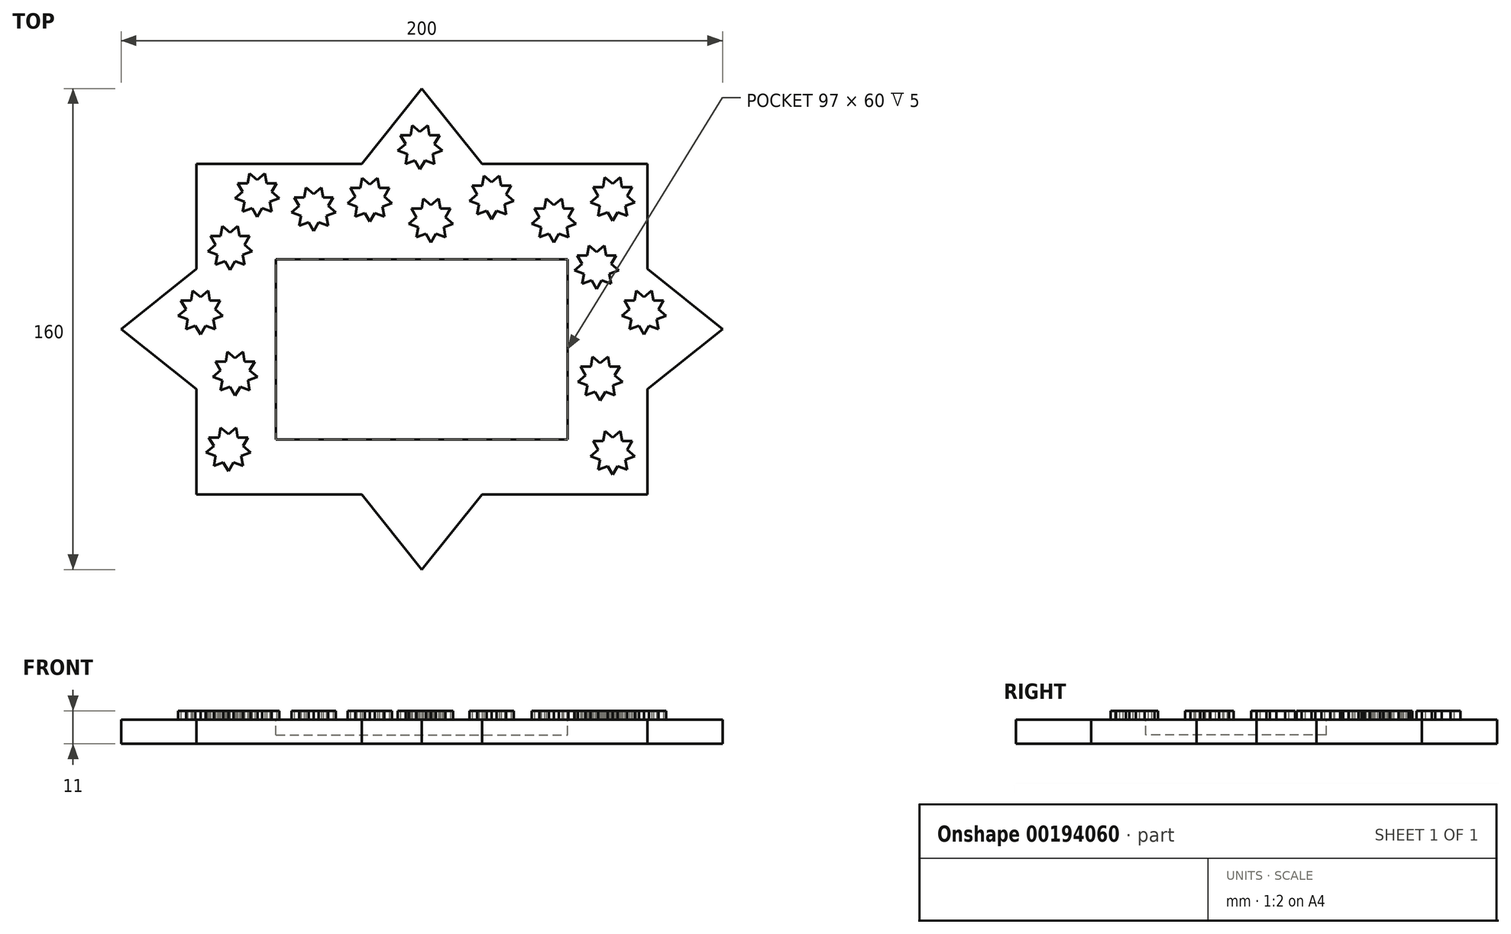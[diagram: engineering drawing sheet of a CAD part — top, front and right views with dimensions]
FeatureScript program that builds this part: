
annotation { "Feature Type Name" : "Feature", "Feature Type Description" : "" }
export const myFeature = defineFeature(function(context is Context, id is Id, definition is map)
    precondition{}
    {
        {
            var Q0;
            Q0=qCreatedBy(makeId("Top.planeOp"),FACE);
            var sketch = newSketch(context, id + "F0", { "sketchPlane" : qUnion([Q0])});
            skLineSegment(sketch, "E0.bottom", {"start": v(75, 55) * mm, "end": v(20, 55) * mm});
            skLineSegment(sketch, "E0.top", {"start": v(75, -55) * mm, "end": v(20, -55) * mm});
            skLineSegment(sketch, "E0.left", {"start": v(75, 55) * mm, "end": v(75, 20) * mm});
            skLineSegment(sketch, "E0.right", {"start": v(-75, 55) * mm, "end": v(-75, 20) * mm});
            skLineSegment(sketch, "E1", {"start": v(75, 20) * mm, "end": v(100, 0) * mm});
            skLineSegment(sketch, "E2", {"start": v(-20, 55) * mm, "end": v(0, 80) * mm});
            skLineSegment(sketch, "E3", {"start": v(0, 80) * mm, "end": v(20, 55) * mm});
            skLineSegment(sketch, "E4.MirrorCS", {"start": v(-20, -55) * mm, "end": v(0, -80) * mm});
            skLineSegment(sketch, "E5.MirrorCS", {"start": v(0, -80) * mm, "end": v(20, -55) * mm});
            skLineSegment(sketch, "E6.MirrorCS", {"start": v(75, -20) * mm, "end": v(100, 0) * mm});
            skLineSegment(sketch, "E7.MirrorCS", {"start": v(-75, 20) * mm, "end": v(-100, 0) * mm});
            skLineSegment(sketch, "E8.MirrorCS", {"start": v(-75, -20) * mm, "end": v(-100, 0) * mm});
            skLineSegment(sketch, "E9.trimOffspring", {"start": v(-75, -20) * mm, "end": v(-75, -55) * mm});
            skLineSegment(sketch, "E10.trimOffspring", {"start": v(75, -20) * mm, "end": v(75, -55) * mm});
            skLineSegment(sketch, "E11.trimOffspring", {"start": v(-20, -55) * mm, "end": v(-75, -55) * mm});
            skLineSegment(sketch, "E12.trimOffspring", {"start": v(-20, 55) * mm, "end": v(-75, 55) * mm});
            skPoint(sketch, "E13.MirrorCS.end.orphan", {"position": v(75, 34.57) * mm});
            skPoint(sketch, "E13.MirrorCS.start.orphan", {"position": v(100, 0) * mm});
            skPoint(sketch, "E14.orphan", {"position": v(75, -34.57) * mm});
            skSolve(sketch);
        }
        {
            var Q0;
            Q0=qSketchRegion(id+"F0",true);
            extrude(context, id + "F1", {"entities" : qUnion([Q0]), "endBound" : BoundingType.SYMMETRIC, "depth" : 8 * mm});
        }
        {
            var Q0;
            Q0=makeQuery(id+"F1.opExtrude","CAP_FACE",FACE,{"disambiguationData":[OSD([sQuery(id+"F0.wireOp",EDGE,"E0.bottom"),sQuery(id+"F0.wireOp",EDGE,"E0.top"),sQuery(id+"F0.wireOp",EDGE,"E0.left"),sQuery(id+"F0.wireOp",EDGE,"E0.right"),sQuery(id+"F0.wireOp",EDGE,"b7ca5f3b-2874-41bd-b902-1c79f96a0a8620.MirrorC"),sQuery(id+"F0.wireOp",EDGE,"b7ca5f3b-2874-41bd-b902-1c79f96a0a8621.MirrorC"),sQuery(id+"F0.wireOp",EDGE,"b7ca5f3b-2874-41bd-b902-1c79f96a0a8622.MirrorCS"),sQuery(id+"F0.wireOp",EDGE,"b7ca5f3b-2874-41bd-b902-1c79f96a0a8623.MirrorCS"),sQuery(id+"F0.wireOp",EDGE,"b7ca5f3b-2874-41bd-b902-1c79f96a0a8624.MirrorCS"),sQuery(id+"F0.wireOp",EDGE,"b7ca5f3b-2874-41bd-b902-1c79f96a0a8625.MirrorCS"),sQuery(id+"F0.wireOp",EDGE,"70034771-ba44-435e-ab74-29499f25fa1546.MirrorC"),sQuery(id+"F0.wireOp",EDGE,"70034771-ba44-435e-ab74-29499f25fa1547.MirrorCS"),sQuery(id+"F0.wireOp",EDGE,"70034771-ba44-435e-ab74-29499f25fa1548.MirrorC"),sQuery(id+"F0.wireOp",EDGE,"70034771-ba44-435e-ab74-29499f25fa1549.MirrorCS"),sQuery(id+"F0.wireOp",EDGE,"70034771-ba44-435e-ab74-29499f25fa1550.MirrorCS"),sQuery(id+"F0.wireOp",EDGE,"70034771-ba44-435e-ab74-29499f25fa1551.MirrorCS"),sQuery(id+"F0.wireOp",EDGE,"E1"),sQuery(id+"F0.wireOp",EDGE,"E2"),sQuery(id+"F0.wireOp",EDGE,"E3"),sQuery(id+"F0.wireOp",EDGE,"E4.MirrorCS"),sQuery(id+"F0.wireOp",EDGE,"E5.MirrorCS"),sQuery(id+"F0.wireOp",EDGE,"E6.MirrorCS"),sQuery(id+"F0.wireOp",EDGE,"E7.MirrorCS"),sQuery(id+"F0.wireOp",EDGE,"E8.MirrorCS"),sQuery(id+"F0.wireOp",EDGE,"E9.trimOffspring"),sQuery(id+"F0.wireOp",EDGE,"E10.trimOffspring"),sQuery(id+"F0.wireOp",EDGE,"E11.trimOffspring"),sQuery(id+"F0.wireOp",EDGE,"E12.trimOffspring")])],"isStart":false});
            var sketch = newSketch(context, id + "F2", { "sketchPlane" : qUnion([Q0])});
            skLineSegment(sketch, "E15.1.17", {"start": v(-32.89, -53.98) * mm, "end": v(-68.5, -53.98) * mm, "construction": true});
            skLineSegment(sketch, "E16.2.0", {"start": v(68.25, 44.34) * mm, "end": v(70.82, 42.19) * mm});
            skLineSegment(sketch, "E16.2.1", {"start": v(61.76, 38.89) * mm, "end": v(58.61, 37.74) * mm});
            skPoint(sketch, "E16.2.2", {"position": v(62.15, 39.96) * mm});
            skCircle(sketch, "E16.2.3", {"center": v(63.43, 43.49) * mm, "radius": 3.75 * mm, "construction": true});
            skLineSegment(sketch, "E16.2.4", {"start": v(56.05, 42.19) * mm, "end": v(58.61, 44.34) * mm});
            skLineSegment(sketch, "E16.2.5", {"start": v(68.25, 37.74) * mm, "end": v(65.1, 38.89) * mm});
            skLineSegment(sketch, "E16.2.6", {"start": v(65.1, 38.89) * mm, "end": v(63.43, 35.99) * mm});
            skLineSegment(sketch, "E16.2.7", {"start": v(69.93, 47.24) * mm, "end": v(68.25, 44.34) * mm});
            skLineSegment(sketch, "E16.2.9", {"start": v(56.94, 47.24) * mm, "end": v(60.29, 47.24) * mm});
            skLineSegment(sketch, "E16.2.10", {"start": v(60.87, 50.54) * mm, "end": v(63.43, 48.38) * mm});
            skLineSegment(sketch, "E16.2.11", {"start": v(60.29, 47.24) * mm, "end": v(60.87, 50.54) * mm});
            skLineSegment(sketch, "E16.2.12", {"start": v(70.82, 42.19) * mm, "end": v(67.67, 41.04) * mm});
            skLineSegment(sketch, "E16.2.13", {"start": v(58.61, 37.74) * mm, "end": v(59.2, 41.04) * mm});
            skLineSegment(sketch, "E16.2.14", {"start": v(58.61, 44.34) * mm, "end": v(56.94, 47.24) * mm});
            skLineSegment(sketch, "E16.2.15", {"start": v(59.2, 41.04) * mm, "end": v(56.05, 42.19) * mm});
            skPoint(sketch, "E16.2.16", {"position": v(66.68, 41.61) * mm});
            skPoint(sketch, "E16.2.18", {"position": v(64.72, 39.96) * mm});
            skLineSegment(sketch, "E16.2.19", {"start": v(63.43, 35.99) * mm, "end": v(61.76, 38.89) * mm});
            skLineSegment(sketch, "E16.2.20", {"start": v(63.43, 48.38) * mm, "end": v(66, 50.54) * mm});
            skLineSegment(sketch, "E16.2.21", {"start": v(67.67, 41.04) * mm, "end": v(68.25, 37.74) * mm});
            skLineSegment(sketch, "E16.2.22", {"start": v(66, 50.54) * mm, "end": v(66.58, 47.24) * mm});
            skLineSegment(sketch, "E16.2.23", {"start": v(66.58, 47.24) * mm, "end": v(69.93, 47.24) * mm});
            skArc(sketch, "E16.2.24", {"start": v(66.68, 41.61) * mm, "mid": v(64.1, 47.18) * mm, "end": v(59.73, 42.88) * mm, "construction": true});
            skArc(sketch, "E16.2.25", {"start": v(62.15, 39.96) * mm, "mid": v(63.43, 39.74) * mm, "end": v(64.72, 39.96) * mm, "construction": true});
            skArc(sketch, "E16.2.26", {"start": v(55.56, 44.8) * mm, "mid": v(71.08, 41.22) * mm, "end": v(56.12, 46.67) * mm, "construction": true});
            skLineSegment(sketch, "E17.2.0", {"start": v(48.77, 37.2) * mm, "end": v(51.34, 35.05) * mm});
            skLineSegment(sketch, "E17.2.1", {"start": v(42.28, 31.75) * mm, "end": v(39.13, 30.6) * mm});
            skPoint(sketch, "E17.2.2", {"position": v(42.67, 32.83) * mm});
            skCircle(sketch, "E17.2.3", {"center": v(43.95, 36.35) * mm, "radius": 3.75 * mm, "construction": true});
            skLineSegment(sketch, "E17.2.4", {"start": v(36.57, 35.05) * mm, "end": v(39.13, 37.2) * mm});
            skLineSegment(sketch, "E17.2.5", {"start": v(48.77, 30.6) * mm, "end": v(45.63, 31.75) * mm});
            skLineSegment(sketch, "E17.2.6", {"start": v(45.63, 31.75) * mm, "end": v(43.95, 28.85) * mm});
            skLineSegment(sketch, "E17.2.7", {"start": v(50.45, 40.1) * mm, "end": v(48.77, 37.2) * mm});
            skLineSegment(sketch, "E17.2.9", {"start": v(37.46, 40.1) * mm, "end": v(40.8, 40.1) * mm});
            skLineSegment(sketch, "E17.2.10", {"start": v(41.39, 43.4) * mm, "end": v(43.95, 41.25) * mm});
            skLineSegment(sketch, "E17.2.11", {"start": v(40.8, 40.1) * mm, "end": v(41.39, 43.4) * mm});
            skLineSegment(sketch, "E17.2.12", {"start": v(51.34, 35.05) * mm, "end": v(48.2, 33.9) * mm});
            skLineSegment(sketch, "E17.2.13", {"start": v(39.13, 30.6) * mm, "end": v(39.71, 33.9) * mm});
            skLineSegment(sketch, "E17.2.14", {"start": v(39.13, 37.2) * mm, "end": v(37.46, 40.1) * mm});
            skLineSegment(sketch, "E17.2.15", {"start": v(39.71, 33.9) * mm, "end": v(36.57, 35.05) * mm});
            skPoint(sketch, "E17.2.16", {"position": v(47.2, 34.47) * mm});
            skPoint(sketch, "E17.2.18", {"position": v(45.23, 32.83) * mm});
            skLineSegment(sketch, "E17.2.19", {"start": v(43.95, 28.85) * mm, "end": v(42.28, 31.75) * mm});
            skLineSegment(sketch, "E17.2.20", {"start": v(43.95, 41.25) * mm, "end": v(46.52, 43.4) * mm});
            skLineSegment(sketch, "E17.2.21", {"start": v(48.2, 33.9) * mm, "end": v(48.77, 30.6) * mm});
            skLineSegment(sketch, "E17.2.22", {"start": v(46.52, 43.4) * mm, "end": v(47.1, 40.1) * mm});
            skLineSegment(sketch, "E17.2.23", {"start": v(47.1, 40.1) * mm, "end": v(50.45, 40.1) * mm});
            skArc(sketch, "E17.2.24", {"start": v(47.2, 34.47) * mm, "mid": v(44.63, 40.04) * mm, "end": v(40.25, 35.74) * mm, "construction": true});
            skArc(sketch, "E17.2.25", {"start": v(42.67, 32.83) * mm, "mid": v(43.95, 32.6) * mm, "end": v(45.23, 32.83) * mm, "construction": true});
            skArc(sketch, "E17.2.26", {"start": v(36.08, 37.66) * mm, "mid": v(51.6, 34.09) * mm, "end": v(36.64, 39.54) * mm, "construction": true});
            skLineSegment(sketch, "E18.2.0", {"start": v(28.05, 44.84) * mm, "end": v(30.62, 42.7) * mm});
            skLineSegment(sketch, "E18.2.1", {"start": v(21.56, 39.4) * mm, "end": v(18.41, 38.25) * mm});
            skPoint(sketch, "E18.2.2", {"position": v(21.95, 40.47) * mm});
            skCircle(sketch, "E18.2.3", {"center": v(23.23, 44) * mm, "radius": 3.75 * mm, "construction": true});
            skLineSegment(sketch, "E18.2.4", {"start": v(15.85, 42.7) * mm, "end": v(18.41, 44.84) * mm});
            skLineSegment(sketch, "E18.2.5", {"start": v(28.05, 38.25) * mm, "end": v(24.9, 39.4) * mm});
            skLineSegment(sketch, "E18.2.6", {"start": v(24.9, 39.4) * mm, "end": v(23.23, 36.5) * mm});
            skLineSegment(sketch, "E18.2.7", {"start": v(29.73, 47.74) * mm, "end": v(28.05, 44.84) * mm});
            skLineSegment(sketch, "E18.2.9", {"start": v(16.74, 47.74) * mm, "end": v(20.09, 47.74) * mm});
            skLineSegment(sketch, "E18.2.10", {"start": v(20.67, 51.04) * mm, "end": v(23.23, 48.89) * mm});
            skLineSegment(sketch, "E18.2.11", {"start": v(20.09, 47.74) * mm, "end": v(20.67, 51.04) * mm});
            skLineSegment(sketch, "E18.2.12", {"start": v(30.62, 42.7) * mm, "end": v(27.47, 41.55) * mm});
            skLineSegment(sketch, "E18.2.13", {"start": v(18.41, 38.25) * mm, "end": v(19, 41.55) * mm});
            skLineSegment(sketch, "E18.2.14", {"start": v(18.41, 44.84) * mm, "end": v(16.74, 47.74) * mm});
            skLineSegment(sketch, "E18.2.15", {"start": v(19, 41.55) * mm, "end": v(15.85, 42.7) * mm});
            skPoint(sketch, "E18.2.16", {"position": v(26.48, 42.12) * mm});
            skPoint(sketch, "E18.2.18", {"position": v(24.52, 40.47) * mm});
            skLineSegment(sketch, "E18.2.19", {"start": v(23.23, 36.5) * mm, "end": v(21.56, 39.4) * mm});
            skLineSegment(sketch, "E18.2.20", {"start": v(23.23, 48.89) * mm, "end": v(25.8, 51.04) * mm});
            skLineSegment(sketch, "E18.2.21", {"start": v(27.47, 41.55) * mm, "end": v(28.05, 38.25) * mm});
            skLineSegment(sketch, "E18.2.22", {"start": v(25.8, 51.04) * mm, "end": v(26.38, 47.74) * mm});
            skLineSegment(sketch, "E18.2.23", {"start": v(26.38, 47.74) * mm, "end": v(29.73, 47.74) * mm});
            skArc(sketch, "E18.2.24", {"start": v(26.48, 42.12) * mm, "mid": v(23.9, 47.68) * mm, "end": v(19.53, 43.39) * mm, "construction": true});
            skArc(sketch, "E18.2.25", {"start": v(21.95, 40.47) * mm, "mid": v(23.23, 40.24) * mm, "end": v(24.52, 40.47) * mm, "construction": true});
            skArc(sketch, "E18.2.26", {"start": v(15.36, 45.3) * mm, "mid": v(30.88, 41.73) * mm, "end": v(15.92, 47.18) * mm, "construction": true});
            skLineSegment(sketch, "E19.2.0", {"start": v(4.22, 61.6) * mm, "end": v(6.78, 59.44) * mm});
            skLineSegment(sketch, "E19.2.1", {"start": v(-2.28, 56.14) * mm, "end": v(-5.42, 55) * mm});
            skPoint(sketch, "E19.2.2", {"position": v(-1.89, 57.22) * mm});
            skCircle(sketch, "E19.2.3", {"center": v(-0.6, 60.74) * mm, "radius": 3.75 * mm, "construction": true});
            skLineSegment(sketch, "E19.2.4", {"start": v(-8, 59.44) * mm, "end": v(-5.42, 61.6) * mm});
            skLineSegment(sketch, "E19.2.5", {"start": v(4.22, 55) * mm, "end": v(1.07, 56.14) * mm});
            skLineSegment(sketch, "E19.2.6", {"start": v(1.07, 56.14) * mm, "end": v(-0.6, 53.24) * mm});
            skLineSegment(sketch, "E19.2.7", {"start": v(5.9, 64.5) * mm, "end": v(4.22, 61.6) * mm});
            skLineSegment(sketch, "E19.2.9", {"start": v(-7.1, 64.5) * mm, "end": v(-3.75, 64.5) * mm});
            skLineSegment(sketch, "E19.2.10", {"start": v(-3.17, 67.79) * mm, "end": v(-0.6, 65.64) * mm});
            skLineSegment(sketch, "E19.2.11", {"start": v(-3.75, 64.5) * mm, "end": v(-3.17, 67.79) * mm});
            skLineSegment(sketch, "E19.2.12", {"start": v(6.78, 59.44) * mm, "end": v(3.64, 58.3) * mm});
            skLineSegment(sketch, "E19.2.13", {"start": v(-5.42, 55) * mm, "end": v(-4.84, 58.3) * mm});
            skLineSegment(sketch, "E19.2.14", {"start": v(-5.42, 61.6) * mm, "end": v(-7.1, 64.5) * mm});
            skLineSegment(sketch, "E19.2.15", {"start": v(-4.84, 58.3) * mm, "end": v(-8, 59.44) * mm});
            skPoint(sketch, "E19.2.16", {"position": v(2.64, 58.87) * mm});
            skPoint(sketch, "E19.2.18", {"position": v(0.68, 57.22) * mm});
            skLineSegment(sketch, "E19.2.19", {"start": v(-0.6, 53.24) * mm, "end": v(-2.28, 56.14) * mm});
            skLineSegment(sketch, "E19.2.20", {"start": v(-0.6, 65.64) * mm, "end": v(1.96, 67.79) * mm});
            skLineSegment(sketch, "E19.2.21", {"start": v(3.64, 58.3) * mm, "end": v(4.22, 55) * mm});
            skLineSegment(sketch, "E19.2.22", {"start": v(1.96, 67.79) * mm, "end": v(2.54, 64.5) * mm});
            skLineSegment(sketch, "E19.2.23", {"start": v(2.54, 64.5) * mm, "end": v(5.9, 64.5) * mm});
            skArc(sketch, "E19.2.24", {"start": v(2.64, 58.87) * mm, "mid": v(-1.95, 64.24) * mm, "end": v(-1.76, 57.17) * mm, "construction": true});
            skArc(sketch, "E19.2.25", {"start": v(-1.89, 57.22) * mm, "mid": v(-0.6, 57) * mm, "end": v(0.68, 57.22) * mm, "construction": true});
            skArc(sketch, "E19.2.26", {"start": v(-6.6, 57.02) * mm, "mid": v(5.77, 63.76) * mm, "end": v(-7.28, 58.47) * mm, "construction": true});
            skLineSegment(sketch, "E20.2.0", {"start": v(7.88, 37.16) * mm, "end": v(10.44, 35.01) * mm});
            skLineSegment(sketch, "E20.2.1", {"start": v(1.38, 31.71) * mm, "end": v(-1.76, 30.57) * mm});
            skPoint(sketch, "E20.2.2", {"position": v(1.77, 32.8) * mm});
            skCircle(sketch, "E20.2.3", {"center": v(3.06, 36.31) * mm, "radius": 3.75 * mm, "construction": true});
            skLineSegment(sketch, "E20.2.4", {"start": v(-4.33, 35.01) * mm, "end": v(-1.76, 37.16) * mm});
            skLineSegment(sketch, "E20.2.5", {"start": v(7.88, 30.57) * mm, "end": v(4.73, 31.71) * mm});
            skLineSegment(sketch, "E20.2.6", {"start": v(4.73, 31.71) * mm, "end": v(3.06, 28.81) * mm});
            skLineSegment(sketch, "E20.2.7", {"start": v(9.55, 40.06) * mm, "end": v(7.88, 37.16) * mm});
            skLineSegment(sketch, "E20.2.9", {"start": v(-3.44, 40.06) * mm, "end": v(-0.1, 40.06) * mm});
            skLineSegment(sketch, "E20.2.10", {"start": v(0.5, 43.36) * mm, "end": v(3.06, 41.21) * mm});
            skLineSegment(sketch, "E20.2.11", {"start": v(-0.1, 40.06) * mm, "end": v(0.5, 43.36) * mm});
            skLineSegment(sketch, "E20.2.12", {"start": v(10.44, 35.01) * mm, "end": v(7.3, 33.87) * mm});
            skLineSegment(sketch, "E20.2.13", {"start": v(-1.76, 30.57) * mm, "end": v(-1.18, 33.87) * mm});
            skLineSegment(sketch, "E20.2.14", {"start": v(-1.76, 37.16) * mm, "end": v(-3.44, 40.06) * mm});
            skLineSegment(sketch, "E20.2.15", {"start": v(-1.18, 33.87) * mm, "end": v(-4.33, 35.01) * mm});
            skPoint(sketch, "E20.2.16", {"position": v(6.3, 34.44) * mm});
            skPoint(sketch, "E20.2.18", {"position": v(4.34, 32.8) * mm});
            skLineSegment(sketch, "E20.2.19", {"start": v(3.06, 28.81) * mm, "end": v(1.38, 31.71) * mm});
            skLineSegment(sketch, "E20.2.20", {"start": v(3.06, 41.21) * mm, "end": v(5.62, 43.36) * mm});
            skLineSegment(sketch, "E20.2.21", {"start": v(7.3, 33.87) * mm, "end": v(7.88, 30.57) * mm});
            skLineSegment(sketch, "E20.2.22", {"start": v(5.62, 43.36) * mm, "end": v(6.2, 40.06) * mm});
            skLineSegment(sketch, "E20.2.23", {"start": v(6.2, 40.06) * mm, "end": v(9.55, 40.06) * mm});
            skArc(sketch, "E20.2.24", {"start": v(6.3, 34.44) * mm, "mid": v(3.73, 40) * mm, "end": v(-0.64, 35.7) * mm, "construction": true});
            skArc(sketch, "E20.2.25", {"start": v(1.77, 32.8) * mm, "mid": v(3.06, 32.56) * mm, "end": v(4.34, 32.8) * mm, "construction": true});
            skArc(sketch, "E20.2.26", {"start": v(-4.81, 37.62) * mm, "mid": v(10.7, 34.05) * mm, "end": v(-4.26, 39.5) * mm, "construction": true});
            skLineSegment(sketch, "E21.2.0", {"start": v(-12.5, 44.08) * mm, "end": v(-9.93, 41.93) * mm});
            skLineSegment(sketch, "E21.2.1", {"start": v(-19, 38.63) * mm, "end": v(-22.14, 37.49) * mm});
            skPoint(sketch, "E21.2.2", {"position": v(-18.6, 39.7) * mm});
            skCircle(sketch, "E21.2.3", {"center": v(-17.32, 43.23) * mm, "radius": 3.75 * mm, "construction": true});
            skLineSegment(sketch, "E21.2.4", {"start": v(-24.7, 41.93) * mm, "end": v(-22.14, 44.08) * mm});
            skLineSegment(sketch, "E21.2.5", {"start": v(-12.5, 37.49) * mm, "end": v(-15.64, 38.63) * mm});
            skLineSegment(sketch, "E21.2.6", {"start": v(-15.64, 38.63) * mm, "end": v(-17.32, 35.73) * mm});
            skLineSegment(sketch, "E21.2.7", {"start": v(-10.82, 46.98) * mm, "end": v(-12.5, 44.08) * mm});
            skLineSegment(sketch, "E21.2.9", {"start": v(-23.81, 46.98) * mm, "end": v(-20.47, 46.98) * mm});
            skLineSegment(sketch, "E21.2.10", {"start": v(-19.88, 50.28) * mm, "end": v(-17.32, 48.13) * mm});
            skLineSegment(sketch, "E21.2.11", {"start": v(-20.47, 46.98) * mm, "end": v(-19.88, 50.28) * mm});
            skLineSegment(sketch, "E21.2.12", {"start": v(-9.93, 41.93) * mm, "end": v(-13.08, 40.78) * mm});
            skLineSegment(sketch, "E21.2.13", {"start": v(-22.14, 37.49) * mm, "end": v(-21.56, 40.78) * mm});
            skLineSegment(sketch, "E21.2.14", {"start": v(-22.14, 44.08) * mm, "end": v(-23.81, 46.98) * mm});
            skLineSegment(sketch, "E21.2.15", {"start": v(-21.56, 40.78) * mm, "end": v(-24.7, 41.93) * mm});
            skPoint(sketch, "E21.2.16", {"position": v(-14.07, 41.36) * mm});
            skPoint(sketch, "E21.2.18", {"position": v(-16.04, 39.7) * mm});
            skLineSegment(sketch, "E21.2.19", {"start": v(-17.32, 35.73) * mm, "end": v(-19, 38.63) * mm});
            skLineSegment(sketch, "E21.2.20", {"start": v(-17.32, 48.13) * mm, "end": v(-14.75, 50.28) * mm});
            skLineSegment(sketch, "E21.2.21", {"start": v(-13.08, 40.78) * mm, "end": v(-12.5, 37.49) * mm});
            skLineSegment(sketch, "E21.2.22", {"start": v(-14.75, 50.28) * mm, "end": v(-14.17, 46.98) * mm});
            skLineSegment(sketch, "E21.2.23", {"start": v(-14.17, 46.98) * mm, "end": v(-10.82, 46.98) * mm});
            skArc(sketch, "E21.2.24", {"start": v(-14.07, 41.36) * mm, "mid": v(-16.65, 46.92) * mm, "end": v(-21.02, 42.62) * mm, "construction": true});
            skArc(sketch, "E21.2.25", {"start": v(-18.6, 39.7) * mm, "mid": v(-17.32, 39.48) * mm, "end": v(-16.04, 39.7) * mm, "construction": true});
            skArc(sketch, "E21.2.26", {"start": v(-25.19, 44.54) * mm, "mid": v(-9.67, 40.97) * mm, "end": v(-24.63, 46.42) * mm, "construction": true});
            skLineSegment(sketch, "E22.2.0", {"start": v(-31.15, 40.93) * mm, "end": v(-28.58, 38.78) * mm});
            skLineSegment(sketch, "E22.2.1", {"start": v(-37.64, 35.48) * mm, "end": v(-40.8, 34.34) * mm});
            skPoint(sketch, "E22.2.2", {"position": v(-37.25, 36.56) * mm});
            skCircle(sketch, "E22.2.3", {"center": v(-35.97, 40.08) * mm, "radius": 3.75 * mm, "construction": true});
            skLineSegment(sketch, "E22.2.4", {"start": v(-43.36, 38.78) * mm, "end": v(-40.8, 40.93) * mm});
            skLineSegment(sketch, "E22.2.5", {"start": v(-31.15, 34.34) * mm, "end": v(-34.3, 35.48) * mm});
            skLineSegment(sketch, "E22.2.6", {"start": v(-34.3, 35.48) * mm, "end": v(-35.97, 32.58) * mm});
            skLineSegment(sketch, "E22.2.7", {"start": v(-29.47, 43.83) * mm, "end": v(-31.15, 40.93) * mm});
            skLineSegment(sketch, "E22.2.9", {"start": v(-42.46, 43.83) * mm, "end": v(-39.12, 43.83) * mm});
            skLineSegment(sketch, "E22.2.10", {"start": v(-38.53, 47.13) * mm, "end": v(-35.97, 44.98) * mm});
            skLineSegment(sketch, "E22.2.11", {"start": v(-39.12, 43.83) * mm, "end": v(-38.53, 47.13) * mm});
            skLineSegment(sketch, "E22.2.12", {"start": v(-28.58, 38.78) * mm, "end": v(-31.73, 37.64) * mm});
            skLineSegment(sketch, "E22.2.13", {"start": v(-40.8, 34.34) * mm, "end": v(-40.2, 37.64) * mm});
            skLineSegment(sketch, "E22.2.14", {"start": v(-40.8, 40.93) * mm, "end": v(-42.46, 43.83) * mm});
            skLineSegment(sketch, "E22.2.15", {"start": v(-40.2, 37.64) * mm, "end": v(-43.36, 38.78) * mm});
            skPoint(sketch, "E22.2.16", {"position": v(-32.72, 38.2) * mm});
            skPoint(sketch, "E22.2.18", {"position": v(-34.69, 36.56) * mm});
            skLineSegment(sketch, "E22.2.19", {"start": v(-35.97, 32.58) * mm, "end": v(-37.64, 35.48) * mm});
            skLineSegment(sketch, "E22.2.20", {"start": v(-35.97, 44.98) * mm, "end": v(-33.4, 47.13) * mm});
            skLineSegment(sketch, "E22.2.21", {"start": v(-31.73, 37.64) * mm, "end": v(-31.15, 34.34) * mm});
            skLineSegment(sketch, "E22.2.22", {"start": v(-33.4, 47.13) * mm, "end": v(-32.82, 43.83) * mm});
            skLineSegment(sketch, "E22.2.23", {"start": v(-32.82, 43.83) * mm, "end": v(-29.47, 43.83) * mm});
            skArc(sketch, "E22.2.24", {"start": v(-32.72, 38.2) * mm, "mid": v(-35.3, 43.77) * mm, "end": v(-39.67, 39.48) * mm, "construction": true});
            skArc(sketch, "E22.2.25", {"start": v(-37.25, 36.56) * mm, "mid": v(-35.97, 36.33) * mm, "end": v(-34.69, 36.56) * mm, "construction": true});
            skArc(sketch, "E22.2.26", {"start": v(-43.84, 41.4) * mm, "mid": v(-28.32, 37.82) * mm, "end": v(-43.28, 43.27) * mm, "construction": true});
            skLineSegment(sketch, "E23.2.0", {"start": v(-49.95, 45.64) * mm, "end": v(-47.38, 43.48) * mm});
            skLineSegment(sketch, "E23.2.1", {"start": v(-56.44, 40.19) * mm, "end": v(-59.59, 39.04) * mm});
            skPoint(sketch, "E23.2.2", {"position": v(-56.05, 41.26) * mm});
            skCircle(sketch, "E23.2.3", {"center": v(-54.77, 44.79) * mm, "radius": 3.75 * mm, "construction": true});
            skLineSegment(sketch, "E23.2.4", {"start": v(-62.15, 43.48) * mm, "end": v(-59.59, 45.64) * mm});
            skLineSegment(sketch, "E23.2.5", {"start": v(-49.95, 39.04) * mm, "end": v(-53.1, 40.19) * mm});
            skLineSegment(sketch, "E23.2.6", {"start": v(-53.1, 40.19) * mm, "end": v(-54.77, 37.29) * mm});
            skLineSegment(sketch, "E23.2.7", {"start": v(-48.27, 48.54) * mm, "end": v(-49.95, 45.64) * mm});
            skLineSegment(sketch, "E23.2.9", {"start": v(-61.26, 48.54) * mm, "end": v(-57.91, 48.54) * mm});
            skLineSegment(sketch, "E23.2.10", {"start": v(-57.33, 51.83) * mm, "end": v(-54.77, 49.68) * mm});
            skLineSegment(sketch, "E23.2.11", {"start": v(-57.91, 48.54) * mm, "end": v(-57.33, 51.83) * mm});
            skLineSegment(sketch, "E23.2.12", {"start": v(-47.38, 43.48) * mm, "end": v(-50.53, 42.34) * mm});
            skLineSegment(sketch, "E23.2.13", {"start": v(-59.59, 39.04) * mm, "end": v(-59, 42.34) * mm});
            skLineSegment(sketch, "E23.2.14", {"start": v(-59.59, 45.64) * mm, "end": v(-61.26, 48.54) * mm});
            skLineSegment(sketch, "E23.2.15", {"start": v(-59, 42.34) * mm, "end": v(-62.15, 43.48) * mm});
            skPoint(sketch, "E23.2.16", {"position": v(-51.52, 42.91) * mm});
            skPoint(sketch, "E23.2.18", {"position": v(-53.48, 41.26) * mm});
            skLineSegment(sketch, "E23.2.19", {"start": v(-54.77, 37.29) * mm, "end": v(-56.44, 40.19) * mm});
            skLineSegment(sketch, "E23.2.20", {"start": v(-54.77, 49.68) * mm, "end": v(-52.2, 51.83) * mm});
            skLineSegment(sketch, "E23.2.21", {"start": v(-50.53, 42.34) * mm, "end": v(-49.95, 39.04) * mm});
            skLineSegment(sketch, "E23.2.22", {"start": v(-52.2, 51.83) * mm, "end": v(-51.62, 48.54) * mm});
            skLineSegment(sketch, "E23.2.23", {"start": v(-51.62, 48.54) * mm, "end": v(-48.27, 48.54) * mm});
            skArc(sketch, "E23.2.24", {"start": v(-51.52, 42.91) * mm, "mid": v(-54.1, 48.48) * mm, "end": v(-58.47, 44.18) * mm, "construction": true});
            skArc(sketch, "E23.2.25", {"start": v(-56.05, 41.26) * mm, "mid": v(-54.77, 41.04) * mm, "end": v(-53.48, 41.26) * mm, "construction": true});
            skArc(sketch, "E23.2.26", {"start": v(-62.64, 46.1) * mm, "mid": v(-47.12, 42.52) * mm, "end": v(-62.08, 47.97) * mm, "construction": true});
            skLineSegment(sketch, "E24.2.0", {"start": v(-58.97, 28) * mm, "end": v(-56.4, 25.85) * mm});
            skLineSegment(sketch, "E24.2.1", {"start": v(-65.46, 22.55) * mm, "end": v(-68.6, 21.4) * mm});
            skPoint(sketch, "E24.2.2", {"position": v(-65.07, 23.63) * mm});
            skCircle(sketch, "E24.2.3", {"center": v(-63.79, 27.15) * mm, "radius": 3.75 * mm, "construction": true});
            skLineSegment(sketch, "E24.2.4", {"start": v(-71.17, 25.85) * mm, "end": v(-68.6, 28) * mm});
            skLineSegment(sketch, "E24.2.5", {"start": v(-58.97, 21.4) * mm, "end": v(-62.11, 22.55) * mm});
            skLineSegment(sketch, "E24.2.6", {"start": v(-62.11, 22.55) * mm, "end": v(-63.79, 19.65) * mm});
            skLineSegment(sketch, "E24.2.7", {"start": v(-57.3, 30.9) * mm, "end": v(-58.97, 28) * mm});
            skLineSegment(sketch, "E24.2.9", {"start": v(-70.28, 30.9) * mm, "end": v(-66.93, 30.9) * mm});
            skLineSegment(sketch, "E24.2.10", {"start": v(-66.35, 34.2) * mm, "end": v(-63.79, 32.05) * mm});
            skLineSegment(sketch, "E24.2.11", {"start": v(-66.93, 30.9) * mm, "end": v(-66.35, 34.2) * mm});
            skLineSegment(sketch, "E24.2.12", {"start": v(-56.4, 25.85) * mm, "end": v(-59.55, 24.7) * mm});
            skLineSegment(sketch, "E24.2.13", {"start": v(-68.6, 21.4) * mm, "end": v(-68.03, 24.7) * mm});
            skLineSegment(sketch, "E24.2.14", {"start": v(-68.6, 28) * mm, "end": v(-70.28, 30.9) * mm});
            skLineSegment(sketch, "E24.2.15", {"start": v(-68.03, 24.7) * mm, "end": v(-71.17, 25.85) * mm});
            skPoint(sketch, "E24.2.16", {"position": v(-60.54, 25.28) * mm});
            skPoint(sketch, "E24.2.18", {"position": v(-62.5, 23.63) * mm});
            skLineSegment(sketch, "E24.2.19", {"start": v(-63.79, 19.65) * mm, "end": v(-65.46, 22.55) * mm});
            skLineSegment(sketch, "E24.2.20", {"start": v(-63.79, 32.05) * mm, "end": v(-61.22, 34.2) * mm});
            skLineSegment(sketch, "E24.2.21", {"start": v(-59.55, 24.7) * mm, "end": v(-58.97, 21.4) * mm});
            skLineSegment(sketch, "E24.2.22", {"start": v(-61.22, 34.2) * mm, "end": v(-60.64, 30.9) * mm});
            skLineSegment(sketch, "E24.2.23", {"start": v(-60.64, 30.9) * mm, "end": v(-57.3, 30.9) * mm});
            skArc(sketch, "E24.2.24", {"start": v(-60.54, 25.28) * mm, "mid": v(-63.11, 30.84) * mm, "end": v(-67.49, 26.54) * mm, "construction": true});
            skArc(sketch, "E24.2.25", {"start": v(-65.07, 23.63) * mm, "mid": v(-63.79, 23.4) * mm, "end": v(-62.5, 23.63) * mm, "construction": true});
            skArc(sketch, "E24.2.26", {"start": v(-71.66, 28.46) * mm, "mid": v(-56.14, 24.89) * mm, "end": v(-71.1, 30.34) * mm, "construction": true});
            skLineSegment(sketch, "E25.2.0", {"start": v(-68.8, 6.6) * mm, "end": v(-66.24, 4.44) * mm});
            skLineSegment(sketch, "E25.2.1", {"start": v(-75.3, 1.15) * mm, "end": v(-78.44, 0) * mm});
            skPoint(sketch, "E25.2.2", {"position": v(-74.9, 2.22) * mm});
            skCircle(sketch, "E25.2.3", {"center": v(-73.62, 5.75) * mm, "radius": 3.75 * mm, "construction": true});
            skLineSegment(sketch, "E25.2.4", {"start": v(-81, 4.44) * mm, "end": v(-78.44, 6.6) * mm});
            skLineSegment(sketch, "E25.2.5", {"start": v(-68.8, 0) * mm, "end": v(-71.95, 1.15) * mm});
            skLineSegment(sketch, "E25.2.6", {"start": v(-71.95, 1.15) * mm, "end": v(-73.62, -1.75) * mm});
            skLineSegment(sketch, "E25.2.7", {"start": v(-67.13, 9.5) * mm, "end": v(-68.8, 6.6) * mm});
            skLineSegment(sketch, "E25.2.9", {"start": v(-80.12, 9.5) * mm, "end": v(-76.77, 9.5) * mm});
            skLineSegment(sketch, "E25.2.10", {"start": v(-76.19, 12.8) * mm, "end": v(-73.62, 10.64) * mm});
            skLineSegment(sketch, "E25.2.11", {"start": v(-76.77, 9.5) * mm, "end": v(-76.19, 12.8) * mm});
            skLineSegment(sketch, "E25.2.12", {"start": v(-66.24, 4.44) * mm, "end": v(-69.38, 3.3) * mm});
            skLineSegment(sketch, "E25.2.13", {"start": v(-78.44, 0) * mm, "end": v(-77.86, 3.3) * mm});
            skLineSegment(sketch, "E25.2.14", {"start": v(-78.44, 6.6) * mm, "end": v(-80.12, 9.5) * mm});
            skLineSegment(sketch, "E25.2.15", {"start": v(-77.86, 3.3) * mm, "end": v(-81, 4.44) * mm});
            skPoint(sketch, "E25.2.16", {"position": v(-70.37, 3.87) * mm});
            skPoint(sketch, "E25.2.18", {"position": v(-72.34, 2.22) * mm});
            skLineSegment(sketch, "E25.2.19", {"start": v(-73.62, -1.75) * mm, "end": v(-75.3, 1.15) * mm});
            skLineSegment(sketch, "E25.2.20", {"start": v(-73.62, 10.64) * mm, "end": v(-71.06, 12.8) * mm});
            skLineSegment(sketch, "E25.2.21", {"start": v(-69.38, 3.3) * mm, "end": v(-68.8, 0) * mm});
            skLineSegment(sketch, "E25.2.22", {"start": v(-71.06, 12.8) * mm, "end": v(-70.47, 9.5) * mm});
            skLineSegment(sketch, "E25.2.23", {"start": v(-70.47, 9.5) * mm, "end": v(-67.13, 9.5) * mm});
            skArc(sketch, "E25.2.24", {"start": v(-70.37, 3.87) * mm, "mid": v(-72.95, 9.43) * mm, "end": v(-77.32, 5.14) * mm, "construction": true});
            skArc(sketch, "E25.2.25", {"start": v(-74.9, 2.22) * mm, "mid": v(-73.62, 2) * mm, "end": v(-72.34, 2.22) * mm, "construction": true});
            skArc(sketch, "E25.2.26", {"start": v(-81.5, 7.05) * mm, "mid": v(-65.97, 3.48) * mm, "end": v(-80.94, 8.93) * mm, "construction": true});
            skLineSegment(sketch, "E26.2.0", {"start": v(-57.25, -13.77) * mm, "end": v(-54.69, -15.92) * mm});
            skLineSegment(sketch, "E26.2.1", {"start": v(-63.75, -19.22) * mm, "end": v(-66.9, -20.36) * mm});
            skPoint(sketch, "E26.2.2", {"position": v(-63.35, -18.14) * mm});
            skCircle(sketch, "E26.2.3", {"center": v(-62.07, -14.62) * mm, "radius": 3.75 * mm, "construction": true});
            skLineSegment(sketch, "E26.2.4", {"start": v(-69.46, -15.92) * mm, "end": v(-66.9, -13.77) * mm});
            skLineSegment(sketch, "E26.2.5", {"start": v(-57.25, -20.36) * mm, "end": v(-60.4, -19.22) * mm});
            skLineSegment(sketch, "E26.2.6", {"start": v(-60.4, -19.22) * mm, "end": v(-62.07, -22.12) * mm});
            skLineSegment(sketch, "E26.2.7", {"start": v(-55.58, -10.87) * mm, "end": v(-57.25, -13.77) * mm});
            skLineSegment(sketch, "E26.2.9", {"start": v(-68.57, -10.87) * mm, "end": v(-65.22, -10.87) * mm});
            skLineSegment(sketch, "E26.2.10", {"start": v(-64.64, -7.57) * mm, "end": v(-62.07, -9.72) * mm});
            skLineSegment(sketch, "E26.2.11", {"start": v(-65.22, -10.87) * mm, "end": v(-64.64, -7.57) * mm});
            skLineSegment(sketch, "E26.2.12", {"start": v(-54.69, -15.92) * mm, "end": v(-57.83, -17.07) * mm});
            skLineSegment(sketch, "E26.2.13", {"start": v(-66.9, -20.36) * mm, "end": v(-66.31, -17.07) * mm});
            skLineSegment(sketch, "E26.2.14", {"start": v(-66.9, -13.77) * mm, "end": v(-68.57, -10.87) * mm});
            skLineSegment(sketch, "E26.2.15", {"start": v(-66.31, -17.07) * mm, "end": v(-69.46, -15.92) * mm});
            skPoint(sketch, "E26.2.16", {"position": v(-58.82, -16.5) * mm});
            skPoint(sketch, "E26.2.18", {"position": v(-60.79, -18.14) * mm});
            skLineSegment(sketch, "E26.2.19", {"start": v(-62.07, -22.12) * mm, "end": v(-63.75, -19.22) * mm});
            skLineSegment(sketch, "E26.2.20", {"start": v(-62.07, -9.72) * mm, "end": v(-59.5, -7.57) * mm});
            skLineSegment(sketch, "E26.2.21", {"start": v(-57.83, -17.07) * mm, "end": v(-57.25, -20.36) * mm});
            skLineSegment(sketch, "E26.2.22", {"start": v(-59.5, -7.57) * mm, "end": v(-58.93, -10.87) * mm});
            skLineSegment(sketch, "E26.2.23", {"start": v(-58.93, -10.87) * mm, "end": v(-55.58, -10.87) * mm});
            skArc(sketch, "E26.2.24", {"start": v(-58.82, -16.5) * mm, "mid": v(-61.4, -10.93) * mm, "end": v(-65.77, -15.23) * mm, "construction": true});
            skArc(sketch, "E26.2.25", {"start": v(-63.35, -18.14) * mm, "mid": v(-62.07, -18.37) * mm, "end": v(-60.79, -18.14) * mm, "construction": true});
            skArc(sketch, "E26.2.26", {"start": v(-69.94, -13.31) * mm, "mid": v(-54.42, -16.88) * mm, "end": v(-69.39, -11.43) * mm, "construction": true});
            skLineSegment(sketch, "E27.2.0", {"start": v(62.94, 21.64) * mm, "end": v(65.5, 19.49) * mm});
            skLineSegment(sketch, "E27.2.1", {"start": v(56.45, 16.19) * mm, "end": v(53.3, 15.04) * mm});
            skPoint(sketch, "E27.2.2", {"position": v(56.84, 17.27) * mm});
            skCircle(sketch, "E27.2.3", {"center": v(58.12, 20.79) * mm, "radius": 3.75 * mm, "construction": true});
            skLineSegment(sketch, "E27.2.4", {"start": v(50.74, 19.49) * mm, "end": v(53.3, 21.64) * mm});
            skLineSegment(sketch, "E27.2.5", {"start": v(62.94, 15.04) * mm, "end": v(59.8, 16.19) * mm});
            skLineSegment(sketch, "E27.2.6", {"start": v(59.8, 16.19) * mm, "end": v(58.12, 13.29) * mm});
            skLineSegment(sketch, "E27.2.7", {"start": v(64.62, 24.54) * mm, "end": v(62.94, 21.64) * mm});
            skLineSegment(sketch, "E27.2.9", {"start": v(51.63, 24.54) * mm, "end": v(54.98, 24.54) * mm});
            skLineSegment(sketch, "E27.2.10", {"start": v(55.56, 27.84) * mm, "end": v(58.12, 25.68) * mm});
            skLineSegment(sketch, "E27.2.11", {"start": v(54.98, 24.54) * mm, "end": v(55.56, 27.84) * mm});
            skLineSegment(sketch, "E27.2.12", {"start": v(65.5, 19.49) * mm, "end": v(62.36, 18.34) * mm});
            skLineSegment(sketch, "E27.2.13", {"start": v(53.3, 15.04) * mm, "end": v(53.88, 18.34) * mm});
            skLineSegment(sketch, "E27.2.14", {"start": v(53.3, 21.64) * mm, "end": v(51.63, 24.54) * mm});
            skLineSegment(sketch, "E27.2.15", {"start": v(53.88, 18.34) * mm, "end": v(50.74, 19.49) * mm});
            skPoint(sketch, "E27.2.16", {"position": v(61.37, 18.91) * mm});
            skPoint(sketch, "E27.2.18", {"position": v(59.4, 17.27) * mm});
            skLineSegment(sketch, "E27.2.19", {"start": v(58.12, 13.29) * mm, "end": v(56.45, 16.19) * mm});
            skLineSegment(sketch, "E27.2.20", {"start": v(58.12, 25.68) * mm, "end": v(60.69, 27.84) * mm});
            skLineSegment(sketch, "E27.2.21", {"start": v(62.36, 18.34) * mm, "end": v(62.94, 15.04) * mm});
            skLineSegment(sketch, "E27.2.22", {"start": v(60.69, 27.84) * mm, "end": v(61.27, 24.54) * mm});
            skLineSegment(sketch, "E27.2.23", {"start": v(61.27, 24.54) * mm, "end": v(64.62, 24.54) * mm});
            skArc(sketch, "E27.2.24", {"start": v(61.37, 18.91) * mm, "mid": v(58.8, 24.48) * mm, "end": v(54.42, 20.18) * mm, "construction": true});
            skArc(sketch, "E27.2.25", {"start": v(56.84, 17.27) * mm, "mid": v(58.12, 17.04) * mm, "end": v(59.4, 17.27) * mm, "construction": true});
            skArc(sketch, "E27.2.26", {"start": v(50.25, 22.1) * mm, "mid": v(65.77, 18.53) * mm, "end": v(50.8, 23.98) * mm, "construction": true});
            skLineSegment(sketch, "E28.2.0", {"start": v(78.7, 6.6) * mm, "end": v(81.27, 4.44) * mm});
            skLineSegment(sketch, "E28.2.1", {"start": v(72.21, 1.15) * mm, "end": v(69.06, 0) * mm});
            skPoint(sketch, "E28.2.2", {"position": v(72.6, 2.22) * mm});
            skCircle(sketch, "E28.2.3", {"center": v(73.89, 5.75) * mm, "radius": 3.75 * mm, "construction": true});
            skLineSegment(sketch, "E28.2.4", {"start": v(66.5, 4.44) * mm, "end": v(69.06, 6.6) * mm});
            skLineSegment(sketch, "E28.2.5", {"start": v(78.7, 0) * mm, "end": v(75.56, 1.15) * mm});
            skLineSegment(sketch, "E28.2.6", {"start": v(75.56, 1.15) * mm, "end": v(73.89, -1.75) * mm});
            skLineSegment(sketch, "E28.2.7", {"start": v(80.38, 9.5) * mm, "end": v(78.7, 6.6) * mm});
            skLineSegment(sketch, "E28.2.9", {"start": v(67.4, 9.5) * mm, "end": v(70.74, 9.5) * mm});
            skLineSegment(sketch, "E28.2.10", {"start": v(71.32, 12.8) * mm, "end": v(73.89, 10.64) * mm});
            skLineSegment(sketch, "E28.2.11", {"start": v(70.74, 9.5) * mm, "end": v(71.32, 12.8) * mm});
            skLineSegment(sketch, "E28.2.12", {"start": v(81.27, 4.44) * mm, "end": v(78.12, 3.3) * mm});
            skLineSegment(sketch, "E28.2.13", {"start": v(69.06, 0) * mm, "end": v(69.65, 3.3) * mm});
            skLineSegment(sketch, "E28.2.14", {"start": v(69.06, 6.6) * mm, "end": v(67.4, 9.5) * mm});
            skLineSegment(sketch, "E28.2.15", {"start": v(69.65, 3.3) * mm, "end": v(66.5, 4.44) * mm});
            skPoint(sketch, "E28.2.16", {"position": v(77.13, 3.87) * mm});
            skPoint(sketch, "E28.2.18", {"position": v(75.17, 2.22) * mm});
            skLineSegment(sketch, "E28.2.19", {"start": v(73.89, -1.75) * mm, "end": v(72.21, 1.15) * mm});
            skLineSegment(sketch, "E28.2.20", {"start": v(73.89, 10.64) * mm, "end": v(76.45, 12.8) * mm});
            skLineSegment(sketch, "E28.2.21", {"start": v(78.12, 3.3) * mm, "end": v(78.7, 0) * mm});
            skLineSegment(sketch, "E28.2.22", {"start": v(76.45, 12.8) * mm, "end": v(77.03, 9.5) * mm});
            skLineSegment(sketch, "E28.2.23", {"start": v(77.03, 9.5) * mm, "end": v(80.38, 9.5) * mm});
            skArc(sketch, "E28.2.24", {"start": v(77.13, 3.87) * mm, "mid": v(74.56, 9.43) * mm, "end": v(70.18, 5.14) * mm, "construction": true});
            skArc(sketch, "E28.2.25", {"start": v(72.6, 2.22) * mm, "mid": v(73.89, 2) * mm, "end": v(75.17, 2.22) * mm, "construction": true});
            skArc(sketch, "E28.2.26", {"start": v(66.01, 7.05) * mm, "mid": v(81.54, 3.48) * mm, "end": v(66.57, 8.93) * mm, "construction": true});
            skLineSegment(sketch, "E29.2.0", {"start": v(64.15, -15.39) * mm, "end": v(66.72, -17.54) * mm});
            skLineSegment(sketch, "E29.2.1", {"start": v(57.66, -20.84) * mm, "end": v(54.51, -21.98) * mm});
            skPoint(sketch, "E29.2.2", {"position": v(58.05, -19.76) * mm});
            skCircle(sketch, "E29.2.3", {"center": v(59.33, -16.24) * mm, "radius": 3.75 * mm, "construction": true});
            skLineSegment(sketch, "E29.2.4", {"start": v(51.95, -17.54) * mm, "end": v(54.51, -15.39) * mm});
            skLineSegment(sketch, "E29.2.5", {"start": v(64.15, -21.98) * mm, "end": v(61, -20.84) * mm});
            skLineSegment(sketch, "E29.2.6", {"start": v(61, -20.84) * mm, "end": v(59.33, -23.74) * mm});
            skLineSegment(sketch, "E29.2.7", {"start": v(65.83, -12.49) * mm, "end": v(64.15, -15.39) * mm});
            skLineSegment(sketch, "E29.2.9", {"start": v(52.84, -12.49) * mm, "end": v(56.18, -12.49) * mm});
            skLineSegment(sketch, "E29.2.10", {"start": v(56.77, -9.2) * mm, "end": v(59.33, -11.34) * mm});
            skLineSegment(sketch, "E29.2.11", {"start": v(56.18, -12.49) * mm, "end": v(56.77, -9.2) * mm});
            skLineSegment(sketch, "E29.2.12", {"start": v(66.72, -17.54) * mm, "end": v(63.57, -18.69) * mm});
            skLineSegment(sketch, "E29.2.13", {"start": v(54.51, -21.98) * mm, "end": v(55.1, -18.69) * mm});
            skLineSegment(sketch, "E29.2.14", {"start": v(54.51, -15.39) * mm, "end": v(52.84, -12.49) * mm});
            skLineSegment(sketch, "E29.2.15", {"start": v(55.1, -18.69) * mm, "end": v(51.95, -17.54) * mm});
            skPoint(sketch, "E29.2.16", {"position": v(62.58, -18.11) * mm});
            skPoint(sketch, "E29.2.18", {"position": v(60.61, -19.76) * mm});
            skLineSegment(sketch, "E29.2.19", {"start": v(59.33, -23.74) * mm, "end": v(57.66, -20.84) * mm});
            skLineSegment(sketch, "E29.2.20", {"start": v(59.33, -11.34) * mm, "end": v(61.9, -9.2) * mm});
            skLineSegment(sketch, "E29.2.21", {"start": v(63.57, -18.69) * mm, "end": v(64.15, -21.98) * mm});
            skLineSegment(sketch, "E29.2.22", {"start": v(61.9, -9.2) * mm, "end": v(62.48, -12.49) * mm});
            skLineSegment(sketch, "E29.2.23", {"start": v(62.48, -12.49) * mm, "end": v(65.83, -12.49) * mm});
            skArc(sketch, "E29.2.24", {"start": v(62.58, -18.11) * mm, "mid": v(60, -12.55) * mm, "end": v(55.63, -16.85) * mm, "construction": true});
            skArc(sketch, "E29.2.25", {"start": v(58.05, -19.76) * mm, "mid": v(59.33, -19.99) * mm, "end": v(60.61, -19.76) * mm, "construction": true});
            skArc(sketch, "E29.2.26", {"start": v(51.46, -14.93) * mm, "mid": v(66.98, -18.5) * mm, "end": v(52.02, -13.05) * mm, "construction": true});
            skLineSegment(sketch, "E30.2.0", {"start": v(-59.52, -38.94) * mm, "end": v(-56.95, -41.1) * mm});
            skLineSegment(sketch, "E30.2.1", {"start": v(-66.01, -44.4) * mm, "end": v(-69.16, -45.54) * mm});
            skPoint(sketch, "E30.2.2", {"position": v(-65.62, -43.32) * mm});
            skCircle(sketch, "E30.2.3", {"center": v(-64.34, -39.8) * mm, "radius": 3.75 * mm, "construction": true});
            skLineSegment(sketch, "E30.2.4", {"start": v(-71.73, -41.1) * mm, "end": v(-69.16, -38.94) * mm});
            skLineSegment(sketch, "E30.2.5", {"start": v(-59.52, -45.54) * mm, "end": v(-62.67, -44.4) * mm});
            skLineSegment(sketch, "E30.2.6", {"start": v(-62.67, -44.4) * mm, "end": v(-64.34, -47.3) * mm});
            skLineSegment(sketch, "E30.2.7", {"start": v(-57.85, -36.04) * mm, "end": v(-59.52, -38.94) * mm});
            skLineSegment(sketch, "E30.2.9", {"start": v(-70.84, -36.04) * mm, "end": v(-67.49, -36.04) * mm});
            skLineSegment(sketch, "E30.2.10", {"start": v(-66.9, -32.75) * mm, "end": v(-64.34, -34.9) * mm});
            skLineSegment(sketch, "E30.2.11", {"start": v(-67.49, -36.04) * mm, "end": v(-66.9, -32.75) * mm});
            skLineSegment(sketch, "E30.2.12", {"start": v(-56.95, -41.1) * mm, "end": v(-60.1, -42.24) * mm});
            skLineSegment(sketch, "E30.2.13", {"start": v(-69.16, -45.54) * mm, "end": v(-68.58, -42.24) * mm});
            skLineSegment(sketch, "E30.2.14", {"start": v(-69.16, -38.94) * mm, "end": v(-70.84, -36.04) * mm});
            skLineSegment(sketch, "E30.2.15", {"start": v(-68.58, -42.24) * mm, "end": v(-71.73, -41.1) * mm});
            skPoint(sketch, "E30.2.16", {"position": v(-61.1, -41.67) * mm});
            skPoint(sketch, "E30.2.18", {"position": v(-63.06, -43.32) * mm});
            skLineSegment(sketch, "E30.2.19", {"start": v(-64.34, -47.3) * mm, "end": v(-66.01, -44.4) * mm});
            skLineSegment(sketch, "E30.2.20", {"start": v(-64.34, -34.9) * mm, "end": v(-61.78, -32.75) * mm});
            skLineSegment(sketch, "E30.2.21", {"start": v(-60.1, -42.24) * mm, "end": v(-59.52, -45.54) * mm});
            skLineSegment(sketch, "E30.2.22", {"start": v(-61.78, -32.75) * mm, "end": v(-61.2, -36.04) * mm});
            skLineSegment(sketch, "E30.2.23", {"start": v(-61.2, -36.04) * mm, "end": v(-57.85, -36.04) * mm});
            skArc(sketch, "E30.2.24", {"start": v(-61.1, -41.67) * mm, "mid": v(-63.67, -36.1) * mm, "end": v(-68.04, -40.4) * mm, "construction": true});
            skArc(sketch, "E30.2.25", {"start": v(-65.62, -43.32) * mm, "mid": v(-64.34, -43.54) * mm, "end": v(-63.06, -43.32) * mm, "construction": true});
            skArc(sketch, "E30.2.26", {"start": v(-72.21, -38.49) * mm, "mid": v(-56.69, -42.06) * mm, "end": v(-71.66, -36.6) * mm, "construction": true});
            skLineSegment(sketch, "E31.2.0", {"start": v(68.3, -40.11) * mm, "end": v(70.86, -42.26) * mm});
            skLineSegment(sketch, "E31.2.1", {"start": v(61.8, -45.56) * mm, "end": v(58.65, -46.7) * mm});
            skPoint(sketch, "E31.2.2", {"position": v(62.19, -44.49) * mm});
            skCircle(sketch, "E31.2.3", {"center": v(63.47, -40.96) * mm, "radius": 3.75 * mm, "construction": true});
            skLineSegment(sketch, "E31.2.4", {"start": v(56.09, -42.26) * mm, "end": v(58.65, -40.11) * mm});
            skLineSegment(sketch, "E31.2.5", {"start": v(68.3, -46.7) * mm, "end": v(65.15, -45.56) * mm});
            skLineSegment(sketch, "E31.2.6", {"start": v(65.15, -45.56) * mm, "end": v(63.47, -48.46) * mm});
            skLineSegment(sketch, "E31.2.7", {"start": v(69.97, -37.21) * mm, "end": v(68.3, -40.11) * mm});
            skLineSegment(sketch, "E31.2.9", {"start": v(56.98, -37.21) * mm, "end": v(60.33, -37.21) * mm});
            skLineSegment(sketch, "E31.2.10", {"start": v(60.9, -33.91) * mm, "end": v(63.47, -36.07) * mm});
            skLineSegment(sketch, "E31.2.11", {"start": v(60.33, -37.21) * mm, "end": v(60.9, -33.91) * mm});
            skLineSegment(sketch, "E31.2.12", {"start": v(70.86, -42.26) * mm, "end": v(67.71, -43.4) * mm});
            skLineSegment(sketch, "E31.2.13", {"start": v(58.65, -46.7) * mm, "end": v(59.23, -43.4) * mm});
            skLineSegment(sketch, "E31.2.14", {"start": v(58.65, -40.11) * mm, "end": v(56.98, -37.21) * mm});
            skLineSegment(sketch, "E31.2.15", {"start": v(59.23, -43.4) * mm, "end": v(56.09, -42.26) * mm});
            skPoint(sketch, "E31.2.16", {"position": v(66.72, -42.84) * mm});
            skPoint(sketch, "E31.2.18", {"position": v(64.75, -44.49) * mm});
            skLineSegment(sketch, "E31.2.19", {"start": v(63.47, -48.46) * mm, "end": v(61.8, -45.56) * mm});
            skLineSegment(sketch, "E31.2.20", {"start": v(63.47, -36.07) * mm, "end": v(66.04, -33.91) * mm});
            skLineSegment(sketch, "E31.2.21", {"start": v(67.71, -43.4) * mm, "end": v(68.3, -46.7) * mm});
            skLineSegment(sketch, "E31.2.22", {"start": v(66.04, -33.91) * mm, "end": v(66.62, -37.21) * mm});
            skLineSegment(sketch, "E31.2.23", {"start": v(66.62, -37.21) * mm, "end": v(69.97, -37.21) * mm});
            skArc(sketch, "E31.2.24", {"start": v(66.72, -42.84) * mm, "mid": v(64.14, -37.27) * mm, "end": v(59.77, -41.57) * mm, "construction": true});
            skArc(sketch, "E31.2.25", {"start": v(62.19, -44.49) * mm, "mid": v(63.47, -44.71) * mm, "end": v(64.75, -44.49) * mm, "construction": true});
            skArc(sketch, "E31.2.26", {"start": v(55.6, -39.65) * mm, "mid": v(71.12, -43.23) * mm, "end": v(56.16, -37.78) * mm, "construction": true});
            skSolve(sketch);
        }
        {
            var Q0;
            Q0=qCreatedBy(makeId("Right.planeOp"),FACE);
            var sketch = newSketch(context, id + "F3", { "sketchPlane" : qUnion([Q0])});
            skLineSegment(sketch, "E32", {"start": v(0, -70.92) * mm, "end": v(0, 69.35) * mm, "construction": true});
            skSolve(sketch);
        }
        {
            var Q0;
            Q0 = qSketchRegion(id + "F2", true);
            extrude(context, id + "F4", {"entities" : qUnion([Q0]), "operationType" : NewBodyOperationType.ADD, "depth" : 3 * mm});
        }
        {
            var Q0;
            Q0=makeQuery(id+"F1.opExtrude","CAP_FACE",FACE,{"disambiguationData":[OSD([sQuery(id+"F0.wireOp",EDGE,"E0.bottom"),sQuery(id+"F0.wireOp",EDGE,"E0.top"),sQuery(id+"F0.wireOp",EDGE,"E0.left"),sQuery(id+"F0.wireOp",EDGE,"E0.right"),sQuery(id+"F0.wireOp",EDGE,"E1"),sQuery(id+"F0.wireOp",EDGE,"E2"),sQuery(id+"F0.wireOp",EDGE,"E3"),sQuery(id+"F0.wireOp",EDGE,"E4.MirrorCS"),sQuery(id+"F0.wireOp",EDGE,"E5.MirrorCS"),sQuery(id+"F0.wireOp",EDGE,"E6.MirrorCS"),sQuery(id+"F0.wireOp",EDGE,"E7.MirrorCS"),sQuery(id+"F0.wireOp",EDGE,"E8.MirrorCS"),sQuery(id+"F0.wireOp",EDGE,"E9.trimOffspring"),sQuery(id+"F0.wireOp",EDGE,"E10.trimOffspring"),sQuery(id+"F0.wireOp",EDGE,"E11.trimOffspring"),sQuery(id+"F0.wireOp",EDGE,"E12.trimOffspring")])],"isStart":false});
            var sketch = newSketch(context, id + "F5", { "sketchPlane" : qUnion([Q0])});
            skLineSegment(sketch, "E33.bottom", {"start": v(-48.5, 23.2) * mm, "end": v(48.5, 23.2) * mm});
            skLineSegment(sketch, "E33.top", {"start": v(-48.5, -36.8) * mm, "end": v(48.5, -36.8) * mm});
            skLineSegment(sketch, "E33.left", {"start": v(-48.5, 23.2) * mm, "end": v(-48.5, -36.8) * mm});
            skLineSegment(sketch, "E33.right", {"start": v(48.5, 23.2) * mm, "end": v(48.5, -36.8) * mm});
            skSolve(sketch);
        }
        {
            var Q0;
            Q0=makeQuery(id+"F5.imprint","IMPRINT",FACE,{"disambiguationData":[TD([[makeQuery(id+"F5.imprint","IMPRINT",EDGE,{"derivedFrom":sQuery(id+"F5.wireOp",EDGE,"E33.bottom")}),-1.0]])]});
            extrude(context, id + "F6", {"entities" : qUnion([Q0]), "operationType" : NewBodyOperationType.REMOVE, "oppositeDirection" : true, "depth" : 5 * mm});
        }
    });
